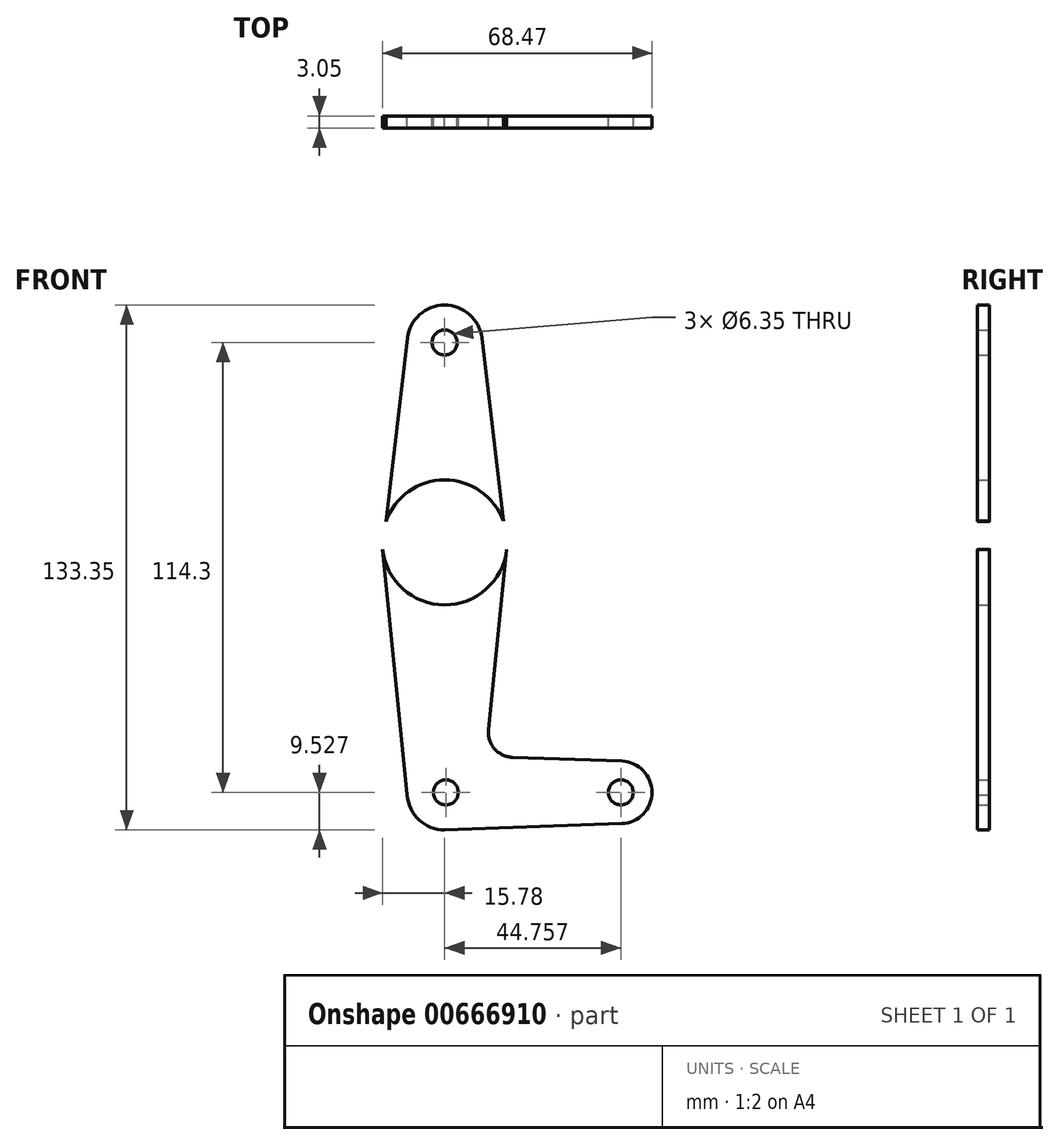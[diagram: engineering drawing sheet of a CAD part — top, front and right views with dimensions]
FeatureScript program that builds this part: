
annotation { "Feature Type Name" : "Feature", "Feature Type Description" : "" }
export const myFeature = defineFeature(function(context is Context, id is Id, definition is map)
    precondition{}
    {
        {
            var Q0;
            Q0=qCreatedBy(makeId("Front.planeOp"),FACE);
            var sketch = newSketch(context, id + "F0", { "sketchPlane" : qUnion([Q0])});
            skLineSegment(sketch, "E0", {"start": v(-2.97, 68.38) * mm, "end": v(-2.97, -45.92) * mm});
            skLineSegment(sketch, "E1", {"start": v(-2.66, -45.92) * mm, "end": v(41.79, -45.92) * mm});
            skCircle(sketch, "E2", {"center": v(-2.97, 68.38) * mm, "radius": 9.52 * mm});
            skCircle(sketch, "E3", {"center": v(-2.97, 17.58) * mm, "radius": 15.88 * mm});
            skCircle(sketch, "E4", {"center": v(-2.97, -45.92) * mm, "radius": 9.53 * mm});
            skCircle(sketch, "E5", {"center": v(41.79, -45.92) * mm, "radius": 7.94 * mm});
            skLineSegment(sketch, "E6", {"start": v(-18.75, 15.83) * mm, "end": v(-12.43, 69.5) * mm});
            skLineSegment(sketch, "E7", {"start": v(12.8, 15.79) * mm, "end": v(6.5, 69.49) * mm});
            skLineSegment(sketch, "E8", {"start": v(8.17, -30.02) * mm, "end": v(12.8, 15.79) * mm});
            skLineSegment(sketch, "E9", {"start": v(-12.47, -46.59) * mm, "end": v(-18.75, 15.83) * mm});
            skLineSegment(sketch, "E10", {"start": v(-2.97, -55.45) * mm, "end": v(42.07, -53.86) * mm});
            skLineSegment(sketch, "E11", {"start": v(14.26, -37) * mm, "end": v(42.07, -38) * mm});
            skCircle(sketch, "E12", {"center": v(-2.97, 68.38) * mm, "radius": 3.18 * mm});
            skCircle(sketch, "E13", {"center": v(-2.97, 17.58) * mm, "radius": 3.18 * mm});
            skCircle(sketch, "E14", {"center": v(-2.66, -45.92) * mm, "radius": 3.18 * mm});
            skCircle(sketch, "E15", {"center": v(41.79, -45.92) * mm, "radius": 3.18 * mm});
            skArc(sketch, "E16.filletArc", {"start": v(8.17, -30.02) * mm, "mid": v(9.7, -34.83) * mm, "end": v(14.26, -37) * mm});
            skSolve(sketch);
        }
        {
            var Q0;
            {var subQ0=sQuery(id+"F0.wireOp",EDGE,"E8");Q0=makeQuery(id+"F0.imprint","IMPRINT",FACE,{"disambiguationData":[TD([[makeQuery(id+"F0.imprint","IMPRINT",EDGE,{"derivedFrom":subQ0}),1.0]])]});}
            var Q1;
            {var subQ0=sQuery(id+"F0.wireOp",EDGE,"E5");var subQ1=sQuery(id+"F0.wireOp",EDGE,"E1");var subQ2=makeQuery(id+"F0.imprint","INTERSECT",VERTEX,{"derivedFrom":[subQ1,subQ0]});Q1=makeQuery(id+"F0.imprint","IMPRINT",FACE,{"disambiguationData":[TD([[makeQuery(id+"F0.imprint","IMPRINT",EDGE,{"disambiguationData":[TD([[subQ2,1.0]])],"derivedFrom":subQ1}),-1.0]])]});}
            var Q2;
            Q2=makeQuery(id+"F0.imprint","IMPRINT",FACE,{"disambiguationData":[TD([[makeQuery(id+"F0.imprint","IMPRINT",EDGE,{"derivedFrom":sQuery(id+"F0.wireOp",EDGE,"E15")}),-1.0]])]});
            var Q3;
            {var subQ5=sQuery(id+"F0.wireOp",EDGE,"E9");Q3=makeQuery(id+"F0.imprint","IMPRINT",FACE,{"disambiguationData":[TD([[makeQuery(id+"F0.imprint","IMPRINT",EDGE,{"derivedFrom":subQ5}),-1.0]])]});}
            var Q4;
            {var subQ0=sQuery(id+"F0.wireOp",EDGE,"E2");var subQ1=sQuery(id+"F0.wireOp",EDGE,"E0");var subQ2=makeQuery(id+"F0.imprint","INTERSECT",VERTEX,{"derivedFrom":[subQ1,subQ0]});Q4=makeQuery(id+"F0.imprint","IMPRINT",FACE,{"disambiguationData":[TD([[makeQuery(id+"F0.imprint","IMPRINT",EDGE,{"disambiguationData":[TD([[subQ2,-1.0]])],"derivedFrom":subQ1}),-1.0]])]});}
            var Q5;
            {var subQ0=sQuery(id+"F0.wireOp",EDGE,"E2");var subQ1=sQuery(id+"F0.wireOp",EDGE,"E0");var subQ2=makeQuery(id+"F0.imprint","INTERSECT",VERTEX,{"derivedFrom":[subQ1,subQ0]});Q5=makeQuery(id+"F0.imprint","IMPRINT",FACE,{"disambiguationData":[TD([[makeQuery(id+"F0.imprint","IMPRINT",EDGE,{"disambiguationData":[TD([[subQ2,-1.0]])],"derivedFrom":subQ1}),1.0]])]});}
            var Q6;
            {var subQ1=sQuery(id+"F0.wireOp",EDGE,"E3");var subQ3=sQuery(id+"F0.wireOp",EDGE,"E0");var subQ8=makeQuery(id+"F0.imprint","INTERSECT",VERTEX,{"disambiguationData":[OD(0.0)],"derivedFrom":[subQ3,subQ1]});Q6=makeQuery(id+"F0.imprint","IMPRINT",FACE,{"disambiguationData":[TD([[makeQuery(id+"F0.imprint","IMPRINT",EDGE,{"disambiguationData":[TD([[subQ8,-1.0]])],"derivedFrom":subQ3}),-1.0]])]});}
            var Q7;
            {var subQ4=sQuery(id+"F0.wireOp",EDGE,"E0");var subQ6=sQuery(id+"F0.wireOp",EDGE,"E14");var subQ10=makeQuery(id+"F0.imprint","INTERSECT",VERTEX,{"derivedFrom":[subQ4,subQ6]});Q7=makeQuery(id+"F0.imprint","IMPRINT",FACE,{"disambiguationData":[TD([[makeQuery(id+"F0.imprint","IMPRINT",EDGE,{"disambiguationData":[TD([[subQ10,1.0]])],"derivedFrom":subQ4}),-1.0]])]});}
            var Q8;
            {var subQ0=sQuery(id+"F0.wireOp",EDGE,"E14");var subQ1=sQuery(id+"F0.wireOp",EDGE,"E0");var subQ2=makeQuery(id+"F0.imprint","INTERSECT",VERTEX,{"derivedFrom":[subQ1,subQ0]});Q8=makeQuery(id+"F0.imprint","IMPRINT",FACE,{"disambiguationData":[TD([[makeQuery(id+"F0.imprint","IMPRINT",EDGE,{"disambiguationData":[TD([[subQ2,1.0]])],"derivedFrom":subQ1}),1.0]])]});}
            var Q9;
            {var subQ1=sQuery(id+"F0.wireOp",EDGE,"E3");var subQ3=sQuery(id+"F0.wireOp",EDGE,"E0");var subQ9=makeQuery(id+"F0.imprint","INTERSECT",VERTEX,{"disambiguationData":[OD(0.0)],"derivedFrom":[subQ3,subQ1]});Q9=makeQuery(id+"F0.imprint","IMPRINT",FACE,{"disambiguationData":[TD([[makeQuery(id+"F0.imprint","IMPRINT",EDGE,{"disambiguationData":[TD([[subQ9,-1.0]])],"derivedFrom":subQ3}),1.0]])]});}
            var Q10;
            Q10=makeQuery(id+"F0.imprint","IMPRINT",FACE,{"disambiguationData":[TD([[makeQuery(id+"F0.imprint","IMPRINT",EDGE,{"derivedFrom":sQuery(id+"F0.wireOp",EDGE,"E12")}),-1.0]])]});
            extrude(context, id + "F1", {"entities" : qUnion([Q0, Q1, Q2, Q3, Q4, Q5, Q6, Q7, Q8, Q9, Q10]), "depth" : 3.05 * mm, "offsetDistance" : 25.4 * mm});
        }
    });
